# Revit family: Franke_A1000_FM_CM_FW(EU)
name_source: partatom
category: Specialty Equipment
revit_build: Autodesk Revit 2015 (Build: 20140606_1530(x64)
units: mm (PartAtom-declared; Revit-internal decimal feet)

## types (8) — shared parameters
Cycle (A1000) = 50 Hz
Cycle Alternative (A1000) = 60 Hz
Depth (mm) = 600 mm
Height (mm) = 796 mm  [stored 2.61155 ft]
Incoming water (cold water) = 8 mm  [stored 0.0262467 ft]
Manufacturer = Franke
Model = A1000 FM CM FW
Noise emission = 70 dB
Number of Protective Conductors (A1000) = 1
URL = https://www.franke.com
Wastewater = 9 mm  [stored 0.0295276 ft]
Water pressure = 800000.0 Pa
Water pressure (with filter) = 600000.0 Pa
Weight = 58 kg
Width (mm) = 340 mm  [stored 1.11549 ft]
zero-valued in all types: Cost

## per-type parameters (varying)
| type | Assembly Code | Description | Energy loss acc. to DIN 18873 (A1000 incl. SU12 FM) | Frontcover | Keynote | Max Overcurrent Protection (A1000) | Number of Nutral Conductors (A1000) | Number of Poles (A1000) | Volts max. (A1000) | Volts min. (A1000) | Watts max. (A1000) | Watts min. (A1000) |
| A1000 FM CM FW(380-415V/black line/EU) | Kaffeevollautomat | Mikroprozessorgesteuerter Kaffeevollautomat mit 2 Präzisionskaffeemühlen | 3.165 kWh/24 h - 400 V 16 A | Franke Black | Kaffeevollautomat | 16 A | 1 | 3 | 415 V | 380 V | 7920 W | 6710 W |
| A1000 FM CM FW(220-240V,2590-3020W/black line/EU) | fully automatic coffee machine | A1000 fully automatic coffee machine | - kWh/24 h - 230 V 16 A | Franke Black | fully automatic coffee machine | 16 A | 1 | 1 | 240 V | 220 V | 3020 W | 2590 W |
| A1000 FM CM FW(220-240V,2590-3020W/anthracite/EU) | fully automatic coffee machine | A1000 fully automatic coffee machine | - kWh/24 h - 230 V 16 A | Franke Anthracite | fully automatic coffee machine | 16 A | 1 | 1 | 240 V | 220 V | 3020 W | 2590 W |
| A1000 FM CM FW(220-240V,4400-5200W/black line/EU) | fully automatic coffee machine | A1000 fully automatic coffee machine | - kWh/24 h - 230 V 16 A | Franke Black | fully automatic coffee machine | 30 A | 1 | 1 | 240 V | 220 V | 5200 W | 4400 W |
| A1000 FM CM FW(220-240V,4400-5200W/anthracite/EU) | fully automatic coffee machine | A1000 fully automatic coffee machine | - kWh/24 h - 230 V 16 A | Franke Anthracite | fully automatic coffee machine | 30 A | 1 | 1 | 240 V | 220 V | 5200 W | 4400 W |
| A1000 FM CM FW(220-240V,5600-7900W/black line/EU) | fully automatic coffee machine | A1000 fully automatic coffee machine | - kWh/24 h - 230 V 16 A | Franke Black | fully automatic coffee machine | 30 A | - | 3 | 240 V | 220 V | 7900 W | 5600 W |
| A1000 FM CM FW(220-240V,5600-7900W/anthracite/EU) | fully automatic coffee machine | A1000 fully automatic coffee machine | - kWh/24 h - 230 V 16 A | Franke Anthracite | fully automatic coffee machine | 30 A | - | 3 | 240 V | 220 V | 7900 W | 5600 W |
| A1000 FM CM FW(380-415V/anthracite/EU) | Kaffeevollautomat | Mikroprozessorgesteuerter Kaffeevollautomat mit 2 Präzisionskaffeemühlen | 3.165 kWh/24 h - 400 V 16 A | Franke Anthracite | Kaffeevollautomat | 16 A | 1 | 3 | 415 V | 380 V | 7920 W | 6710 W |

note: [stored X ft] marks values corroborated as IEEE doubles in the binary element streams (Revit-internal decimal feet)

## geometry (parser evidence)
native form markers: Extrusion x1
no freeform markers — native parametric forms only
